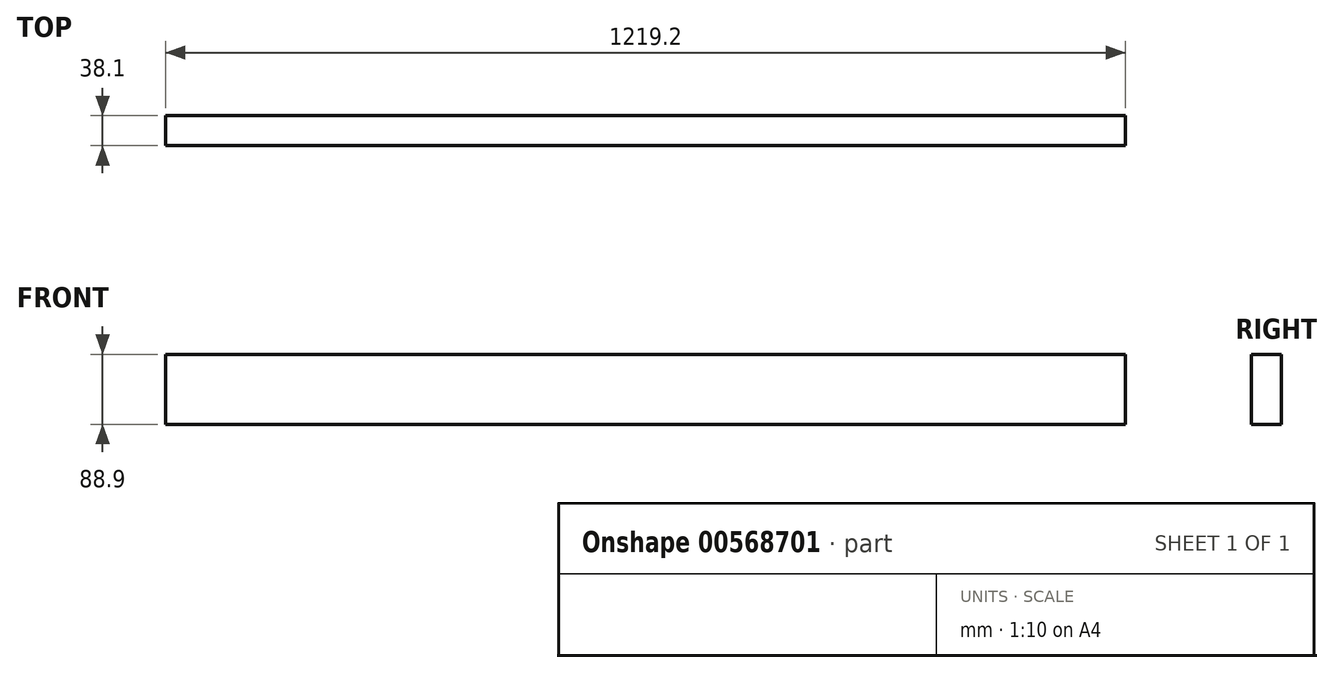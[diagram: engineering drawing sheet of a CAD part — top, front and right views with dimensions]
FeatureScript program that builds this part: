
annotation { "Feature Type Name" : "Feature", "Feature Type Description" : "" }
export const myFeature = defineFeature(function(context is Context, id is Id, definition is map)
    precondition{}
    {
        {
            var Q0;
            Q0=qCreatedBy(makeId("Top.planeOp"),FACE);
            var sketch = newSketch(context, id + "F0", { "sketchPlane" : qUnion([Q0])});
            skLineSegment(sketch, "E0.bottom", {"start": v(-609.6, -19.05) * mm, "end": v(609.6, -19.05) * mm});
            skLineSegment(sketch, "E0.top", {"start": v(-609.6, 19.05) * mm, "end": v(609.6, 19.05) * mm});
            skLineSegment(sketch, "E0.left", {"start": v(-609.6, -19.05) * mm, "end": v(-609.6, 19.05) * mm});
            skLineSegment(sketch, "E0.right", {"start": v(609.6, -19.05) * mm, "end": v(609.6, 19.05) * mm});
            skPoint(sketch, "E0.middle", {"position": v(0, 0) * mm});
            skSolve(sketch);
        }
        {
            var Q0;
            Q0 = qSketchRegion(id + "F0", true);
            extrude(context, id + "F1", {"entities" : qUnion([Q0]), "depth" : 88.9 * mm, "offsetDistance" : 25.4 * mm});
        }
    });
